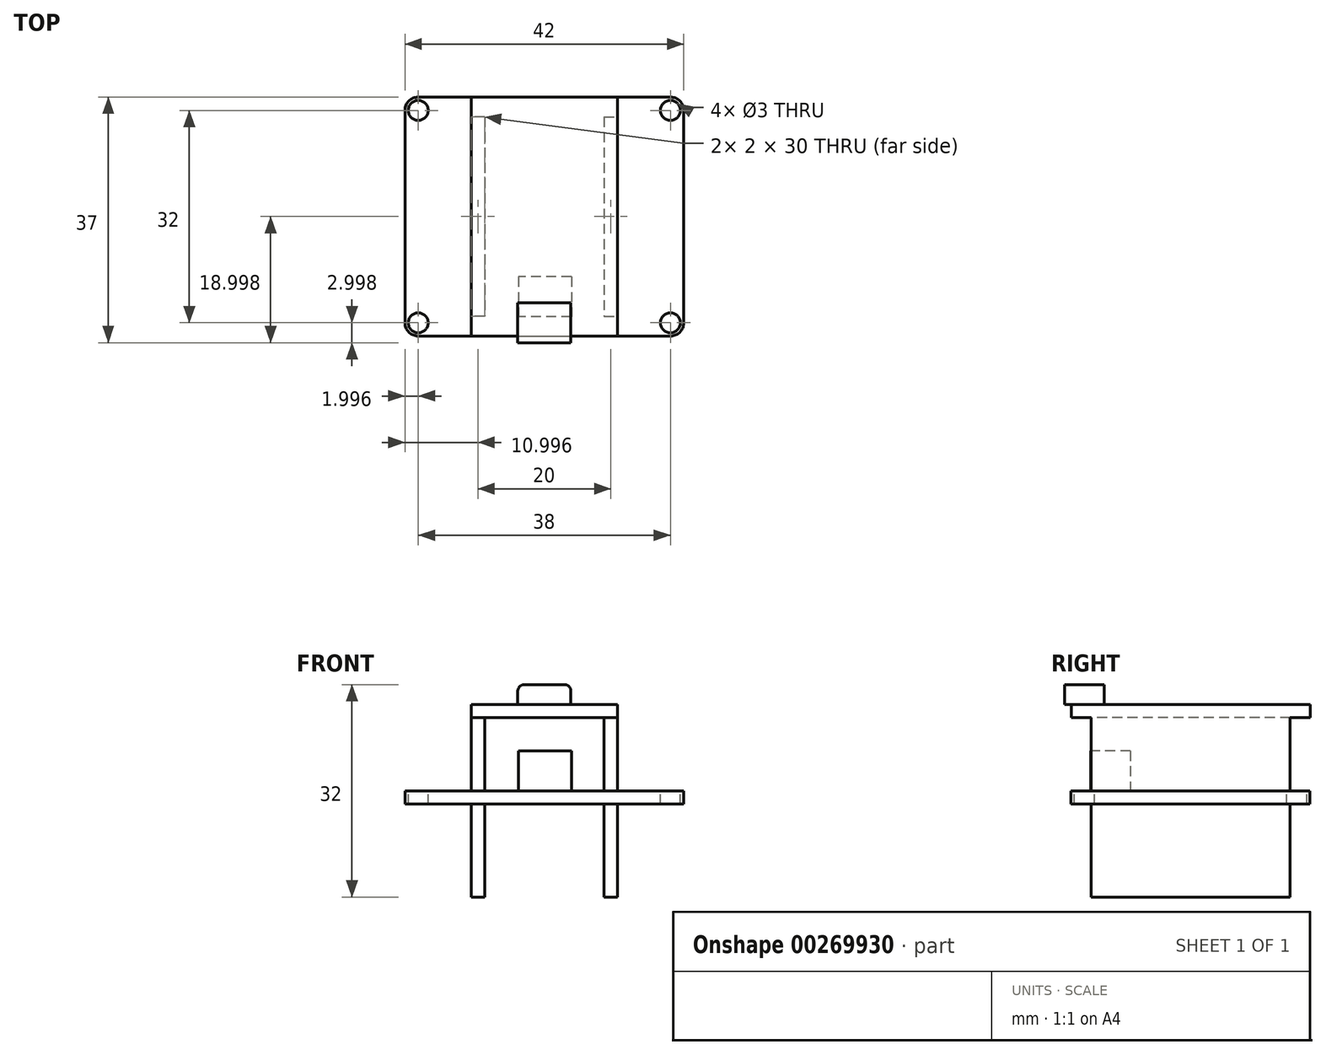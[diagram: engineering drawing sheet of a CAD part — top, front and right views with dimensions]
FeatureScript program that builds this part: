
annotation { "Feature Type Name" : "Feature", "Feature Type Description" : "" }
export const myFeature = defineFeature(function(context is Context, id is Id, definition is map)
    precondition{}
    {
        {
            var Q0;
            Q0=qCreatedBy(makeId("Top.planeOp"),FACE);
            var sketch = newSketch(context, id + "F0", { "sketchPlane" : qUnion([Q0])});
            skLineSegment(sketch, "E0.bottom", {"start": v(-14.25, 12.56) * mm, "end": v(27.75, 12.56) * mm});
            skLineSegment(sketch, "E0.top", {"start": v(-14.25, -23.44) * mm, "end": v(27.75, -23.44) * mm});
            skLineSegment(sketch, "E0.left", {"start": v(-14.25, 12.56) * mm, "end": v(-14.25, -23.44) * mm});
            skLineSegment(sketch, "E0.right", {"start": v(27.75, 12.56) * mm, "end": v(27.75, -23.44) * mm});
            skSolve(sketch);
        }
        {
            var Q0;
            Q0=makeQuery(id+"F0.imprint","IMPRINT",FACE,{"disambiguationData":[TD([[makeQuery(id+"F0.imprint","IMPRINT",EDGE,{"derivedFrom":sQuery(id+"F0.wireOp",EDGE,"E0.bottom")}),-1.0]])]});
            extrude(context, id + "F1", {"entities" : qUnion([Q0]), "depth" : 2 * mm});
        }
        {
            var Q0;
            Q0=makeQuery(id+"F1.opExtrude","SWEPT_EDGE",EDGE,{"disambiguationData":[OSD([sQuery(id+"F0.wireOp",EDGE,"E0.top"),sQuery(id+"F0.wireOp",EDGE,"E0.right")])]});
            var Q1;
            Q1=makeQuery(id+"F1.opExtrude","SWEPT_EDGE",EDGE,{"disambiguationData":[OSD([sQuery(id+"F0.wireOp",EDGE,"E0.bottom"),sQuery(id+"F0.wireOp",EDGE,"E0.right")])]});
            var Q2;
            Q2=makeQuery(id+"F1.opExtrude","SWEPT_EDGE",EDGE,{"disambiguationData":[OSD([sQuery(id+"F0.wireOp",EDGE,"E0.top"),sQuery(id+"F0.wireOp",EDGE,"E0.left")])]});
            var Q3;
            Q3=makeQuery(id+"F1.opExtrude","SWEPT_EDGE",EDGE,{"disambiguationData":[OSD([sQuery(id+"F0.wireOp",EDGE,"E0.bottom"),sQuery(id+"F0.wireOp",EDGE,"E0.left")])]});
            fillet(context, id + "F2", {"entities" : qUnion([Q0, Q1, Q2, Q3]), "radius" : 2 * mm, "tangentPropagation" : true, "allowEdgeOverflow" : false});
        }
        {
            var Q0;
            Q0=makeQuery(id+"F1.opExtrude","CAP_FACE",FACE,{"disambiguationData":[OSD([sQuery(id+"F0.wireOp",EDGE,"E0.bottom"),sQuery(id+"F0.wireOp",EDGE,"E0.top"),sQuery(id+"F0.wireOp",EDGE,"E0.left"),sQuery(id+"F0.wireOp",EDGE,"E0.right")])],"isStart":false});
            var sketch = newSketch(context, id + "F3", { "sketchPlane" : qUnion([Q0])});
            skCircle(sketch, "E1", {"center": v(25.75, 10.56) * mm, "radius": 1.5 * mm});
            skCircle(sketch, "E2", {"center": v(-12.25, 10.56) * mm, "radius": 1.5 * mm});
            skCircle(sketch, "E3", {"center": v(-12.25, -21.44) * mm, "radius": 1.5 * mm});
            skCircle(sketch, "E4", {"center": v(25.75, -21.44) * mm, "radius": 1.5 * mm});
            skSolve(sketch);
        }
        {
            var Q0;
            Q0=makeQuery(id+"F3.imprint","IMPRINT",FACE,{"disambiguationData":[TD([[makeQuery(id+"F3.imprint","IMPRINT",EDGE,{"derivedFrom":sQuery(id+"F3.wireOp",EDGE,"E2")}),1.0]])]});
            var Q1;
            Q1=makeQuery(id+"F3.imprint","IMPRINT",FACE,{"disambiguationData":[TD([[makeQuery(id+"F3.imprint","IMPRINT",EDGE,{"derivedFrom":sQuery(id+"F3.wireOp",EDGE,"E3")}),1.0]])]});
            var Q2;
            Q2=makeQuery(id+"F3.imprint","IMPRINT",FACE,{"disambiguationData":[TD([[makeQuery(id+"F3.imprint","IMPRINT",EDGE,{"derivedFrom":sQuery(id+"F3.wireOp",EDGE,"E4")}),1.0]])]});
            var Q3;
            Q3=makeQuery(id+"F3.imprint","IMPRINT",FACE,{"disambiguationData":[TD([[makeQuery(id+"F3.imprint","IMPRINT",EDGE,{"derivedFrom":sQuery(id+"F3.wireOp",EDGE,"E1")}),1.0]])]});
            extrude(context, id + "F4", {"entities" : qUnion([Q0, Q1, Q2, Q3]), "operationType" : NewBodyOperationType.REMOVE, "oppositeDirection" : true, "depth" : 2 * mm});
        }
        {
            var Q0;
            Q0=makeQuery(id+"F1.opExtrude","CAP_FACE",FACE,{"disambiguationData":[OSD([sQuery(id+"F0.wireOp",EDGE,"E0.bottom"),sQuery(id+"F0.wireOp",EDGE,"E0.top"),sQuery(id+"F0.wireOp",EDGE,"E0.left"),sQuery(id+"F0.wireOp",EDGE,"E0.right")])],"isStart":true});
            var sketch = newSketch(context, id + "F5", { "sketchPlane" : qUnion([Q0])});
            skLineSegment(sketch, "E5", {"start": v(-22.63, 5.44) * mm, "end": v(40.2, 5.44) * mm, "construction": true});
            skPoint(sketch, "E5.startSnap0", {"position": v(-14.25, 5.44) * mm});
            skPoint(sketch, "E6.middle", {"position": v(-4.25, 5.44) * mm});
            skLineSegment(sketch, "E7", {"start": v(6.75, -17.67) * mm, "end": v(6.75, 26.9) * mm, "construction": true});
            skPoint(sketch, "E7.startSnap0", {"position": v(6.75, -12.56) * mm});
            skPoint(sketch, "E7.endSnap0", {"position": v(6.75, 23.44) * mm});
            skLineSegment(sketch, "E8.MirrorCS", {"start": v(15.75, 20.44) * mm, "end": v(17.75, 20.44) * mm});
            skLineSegment(sketch, "E9.MirrorCS", {"start": v(15.75, -9.56) * mm, "end": v(15.75, 20.44) * mm});
            skLineSegment(sketch, "E10.MirrorCS", {"start": v(15.75, -9.56) * mm, "end": v(17.75, -9.56) * mm});
            skLineSegment(sketch, "E11.MirrorCS", {"start": v(17.75, -9.56) * mm, "end": v(17.75, 20.44) * mm});
            skLineSegment(sketch, "E12.MirrorCS", {"start": v(-2.25, 20.44) * mm, "end": v(-4.25, 20.44) * mm});
            skLineSegment(sketch, "E13.MirrorCS", {"start": v(-4.25, -9.56) * mm, "end": v(-4.25, 20.44) * mm});
            skLineSegment(sketch, "E14.MirrorCS", {"start": v(-2.25, -9.56) * mm, "end": v(-2.25, 20.44) * mm});
            skLineSegment(sketch, "E15.MirrorCS", {"start": v(-2.25, -9.56) * mm, "end": v(-4.25, -9.56) * mm});
            skSolve(sketch);
        }
        {
            var Q0;
            Q0=makeQuery(id+"F5.imprint","IMPRINT",FACE,{"disambiguationData":[TD([[makeQuery(id+"F5.imprint","IMPRINT",EDGE,{"derivedFrom":sQuery(id+"F5.wireOp",EDGE,"E6.bottom")}),-1.0]])]});
            var Q1;
            Q1=makeQuery(id+"F5.imprint","IMPRINT",FACE,{"disambiguationData":[TD([[makeQuery(id+"F5.imprint","IMPRINT",EDGE,{"derivedFrom":sQuery(id+"F5.wireOp",EDGE,"E8.MirrorCS")}),-1.0]])]});
            var Q2;
            Q2=makeQuery(id+"F5.imprint","IMPRINT",FACE,{"disambiguationData":[TD([[makeQuery(id+"F5.imprint","IMPRINT",EDGE,{"derivedFrom":sQuery(id+"F5.wireOp",EDGE,"E12.MirrorCS")}),1.0]])]});
            extrude(context, id + "F6", {"entities" : qUnion([Q0, Q1, Q2]), "operationType" : NewBodyOperationType.ADD, "depth" : 14 * mm});
        }
        {
            var Q0;
            Q0=makeQuery(id+"F1.opExtrude","CAP_FACE",FACE,{"disambiguationData":[OSD([sQuery(id+"F0.wireOp",EDGE,"E0.bottom"),sQuery(id+"F0.wireOp",EDGE,"E0.top"),sQuery(id+"F0.wireOp",EDGE,"E0.left"),sQuery(id+"F0.wireOp",EDGE,"E0.right")])],"isStart":false});
            var sketch = newSketch(context, id + "F7", { "sketchPlane" : qUnion([Q0])});
            skLineSegment(sketch, "E16.4", {"start": v(15.75, 9.56) * mm, "end": v(17.75, 9.56) * mm});
            skLineSegment(sketch, "E16.5", {"start": v(15.75, 9.56) * mm, "end": v(15.75, -20.44) * mm});
            skLineSegment(sketch, "E16.6", {"start": v(17.75, 9.56) * mm, "end": v(17.75, -20.44) * mm});
            skLineSegment(sketch, "E16.7", {"start": v(15.75, -20.44) * mm, "end": v(17.75, -20.44) * mm});
            skLineSegment(sketch, "E17.MirrorCS", {"start": v(-2.25, 9.56) * mm, "end": v(-4.25, 9.56) * mm});
            skLineSegment(sketch, "E18.MirrorCS", {"start": v(-2.25, 9.56) * mm, "end": v(-2.25, -20.44) * mm});
            skLineSegment(sketch, "E19.MirrorCS", {"start": v(-4.25, 9.56) * mm, "end": v(-4.25, -20.44) * mm});
            skLineSegment(sketch, "E20.MirrorCS", {"start": v(-2.25, -20.44) * mm, "end": v(-4.25, -20.44) * mm});
            skLineSegment(sketch, "E21.bottom", {"start": v(10.83, -14.51) * mm, "end": v(2.83, -14.51) * mm});
            skLineSegment(sketch, "E21.top", {"start": v(10.83, -20.51) * mm, "end": v(2.83, -20.51) * mm});
            skLineSegment(sketch, "E21.left", {"start": v(10.83, -14.51) * mm, "end": v(10.83, -20.51) * mm});
            skLineSegment(sketch, "E21.right", {"start": v(2.83, -14.51) * mm, "end": v(2.83, -20.51) * mm});
            skPoint(sketch, "E21.middle", {"position": v(4.43, -19.51) * mm});
            skSolve(sketch);
        }
        {
            var Q0;
            Q0=makeQuery(id+"F7.imprint","IMPRINT",FACE,{"disambiguationData":[TD([[makeQuery(id+"F7.imprint","IMPRINT",EDGE,{"derivedFrom":sQuery(id+"F7.wireOp",EDGE,"E16.0")}),1.0]])]});
            var Q1;
            Q1=makeQuery(id+"F7.imprint","IMPRINT",FACE,{"disambiguationData":[TD([[makeQuery(id+"F7.imprint","IMPRINT",EDGE,{"derivedFrom":sQuery(id+"F7.wireOp",EDGE,"E16.4")}),-1.0]])]});
            var Q2;
            Q2=makeQuery(id+"F7.imprint","IMPRINT",FACE,{"disambiguationData":[TD([[makeQuery(id+"F7.imprint","IMPRINT",EDGE,{"derivedFrom":sQuery(id+"F7.wireOp",EDGE,"E17.MirrorCS")}),1.0]])]});
            extrude(context, id + "F8", {"entities" : qUnion([Q0, Q1, Q2]), "operationType" : NewBodyOperationType.ADD, "depth" : 11 * mm});
        }
        {
            var Q0;
            Q0=makeQuery(id+"F8.opExtrude","CAP_FACE",FACE,{"disambiguationData":[OSD([sQuery(id+"F7.wireOp",EDGE,"E17.MirrorCS"),sQuery(id+"F7.wireOp",EDGE,"E18.MirrorCS"),sQuery(id+"F7.wireOp",EDGE,"E19.MirrorCS"),sQuery(id+"F7.wireOp",EDGE,"E20.MirrorCS")])],"isStart":false});
            var sketch = newSketch(context, id + "F9", { "sketchPlane" : qUnion([Q0])});
            skLineSegment(sketch, "E22.bottom", {"start": v(-4.25, 12.56) * mm, "end": v(17.75, 12.56) * mm});
            skLineSegment(sketch, "E22.top", {"start": v(-4.25, -23.44) * mm, "end": v(17.75, -23.44) * mm});
            skLineSegment(sketch, "E22.left", {"start": v(-4.25, 12.56) * mm, "end": v(-4.25, -23.44) * mm});
            skLineSegment(sketch, "E22.right", {"start": v(17.75, 12.56) * mm, "end": v(17.75, -23.44) * mm});
            skSolve(sketch);
        }
        {
            var Q0;
            Q0 = qSketchRegion(id + "F9", true);
            extrude(context, id + "F10", {"entities" : qUnion([Q0]), "operationType" : NewBodyOperationType.ADD, "depth" : 2 * mm});
        }
        {
            var Q0;
            Q0=makeQuery(id+"F10.opExtrude","CAP_FACE",FACE,{"disambiguationData":[OSD([sQuery(id+"F9.wireOp",EDGE,"E22.bottom"),sQuery(id+"F9.wireOp",EDGE,"E22.top"),sQuery(id+"F9.wireOp",EDGE,"E22.left"),sQuery(id+"F9.wireOp",EDGE,"E22.right")])],"isStart":false});
            var sketch = newSketch(context, id + "F11", { "sketchPlane" : qUnion([Q0])});
            skLineSegment(sketch, "E23.bottom", {"start": v(10.75, -24.44) * mm, "end": v(2.75, -24.44) * mm});
            skLineSegment(sketch, "E23.top", {"start": v(10.75, -18.44) * mm, "end": v(2.75, -18.44) * mm});
            skLineSegment(sketch, "E23.left", {"start": v(10.75, -24.44) * mm, "end": v(10.75, -18.44) * mm});
            skLineSegment(sketch, "E23.right", {"start": v(2.75, -24.44) * mm, "end": v(2.75, -18.44) * mm});
            skPoint(sketch, "E23.middle", {"position": v(6.75, -23.44) * mm});
            skSolve(sketch);
        }
        {
            var Q0;
            {var subQ0=sQuery(id+"F11.wireOp",EDGE,"E23.top");Q0=makeQuery(id+"F11.imprint","IMPRINT",FACE,{"disambiguationData":[TD([[makeQuery(id+"F11.imprint","IMPRINT",EDGE,{"derivedFrom":subQ0}),1.0]])]});}
            var Q1;
            {var subQ0=sQuery(id+"F11.wireOp",EDGE,"E23.bottom");Q1=makeQuery(id+"F11.imprint","IMPRINT",FACE,{"disambiguationData":[TD([[makeQuery(id+"F11.imprint","IMPRINT",EDGE,{"derivedFrom":subQ0}),-1.0]])]});}
            extrude(context, id + "F12", {"entities" : qUnion([Q0, Q1]), "operationType" : NewBodyOperationType.ADD, "depth" : 3 * mm});
        }
        {
            var Q0;
            Q0=makeQuery(id+"F12.opExtrude","CAP_EDGE",EDGE,{"disambiguationData":[OSD([sQuery(id+"F11.wireOp",EDGE,"E23.left")])],"isStart":false});
            var Q1;
            Q1=makeQuery(id+"F12.opExtrude","CAP_EDGE",EDGE,{"disambiguationData":[OSD([sQuery(id+"F11.wireOp",EDGE,"E23.right")])],"isStart":false});
            fillet(context, id + "F13", {"entities" : qUnion([Q0, Q1]), "radius" : 1 * mm, "tangentPropagation" : true, "allowEdgeOverflow" : false});
        }
        {
            var Q0;
            Q0=makeQuery(id+"F7.imprint","IMPRINT",FACE,{"disambiguationData":[TD([[makeQuery(id+"F7.imprint","IMPRINT",EDGE,{"derivedFrom":sQuery(id+"F7.wireOp",EDGE,"E21.bottom")}),1.0]])]});
            extrude(context, id + "F14", {"entities" : qUnion([Q0]), "operationType" : NewBodyOperationType.ADD, "depth" : 6 * mm});
        }
        {
            var Q0;
            Q0=makeQuery(id+"F1.opExtrude","SWEPT_BODY",BODY,{"disambiguationData":[OSD([sQuery(id+"F0.wireOp",EDGE,"E0.bottom"),sQuery(id+"F0.wireOp",EDGE,"E0.top"),sQuery(id+"F0.wireOp",EDGE,"E0.left"),sQuery(id+"F0.wireOp",EDGE,"E0.right")])]});
            transform(context, id + "F15", {"entities" : qUnion([Q0]), "transformType" : TransformType.TRANSLATION_3D, "dx" : 0 * mm, "dy" : 0 * mm, "dz" : 0 * mm, "makeCopy" : true});
        }
        {
            var Q0;
            Q0=makeQuery(id+"F15.opPattern","COPY",BODY,{"derivedFrom":makeQuery(id+"F1.opExtrude","SWEPT_BODY",BODY,{"disambiguationData":[OSD([sQuery(id+"F0.wireOp",EDGE,"E0.bottom"),sQuery(id+"F0.wireOp",EDGE,"E0.top"),sQuery(id+"F0.wireOp",EDGE,"E0.left"),sQuery(id+"F0.wireOp",EDGE,"E0.right")])]}),"instanceName":"1"});
            deleteBodies(context, id + "F16", {"entities" : qUnion([Q0])});
        }
    });
